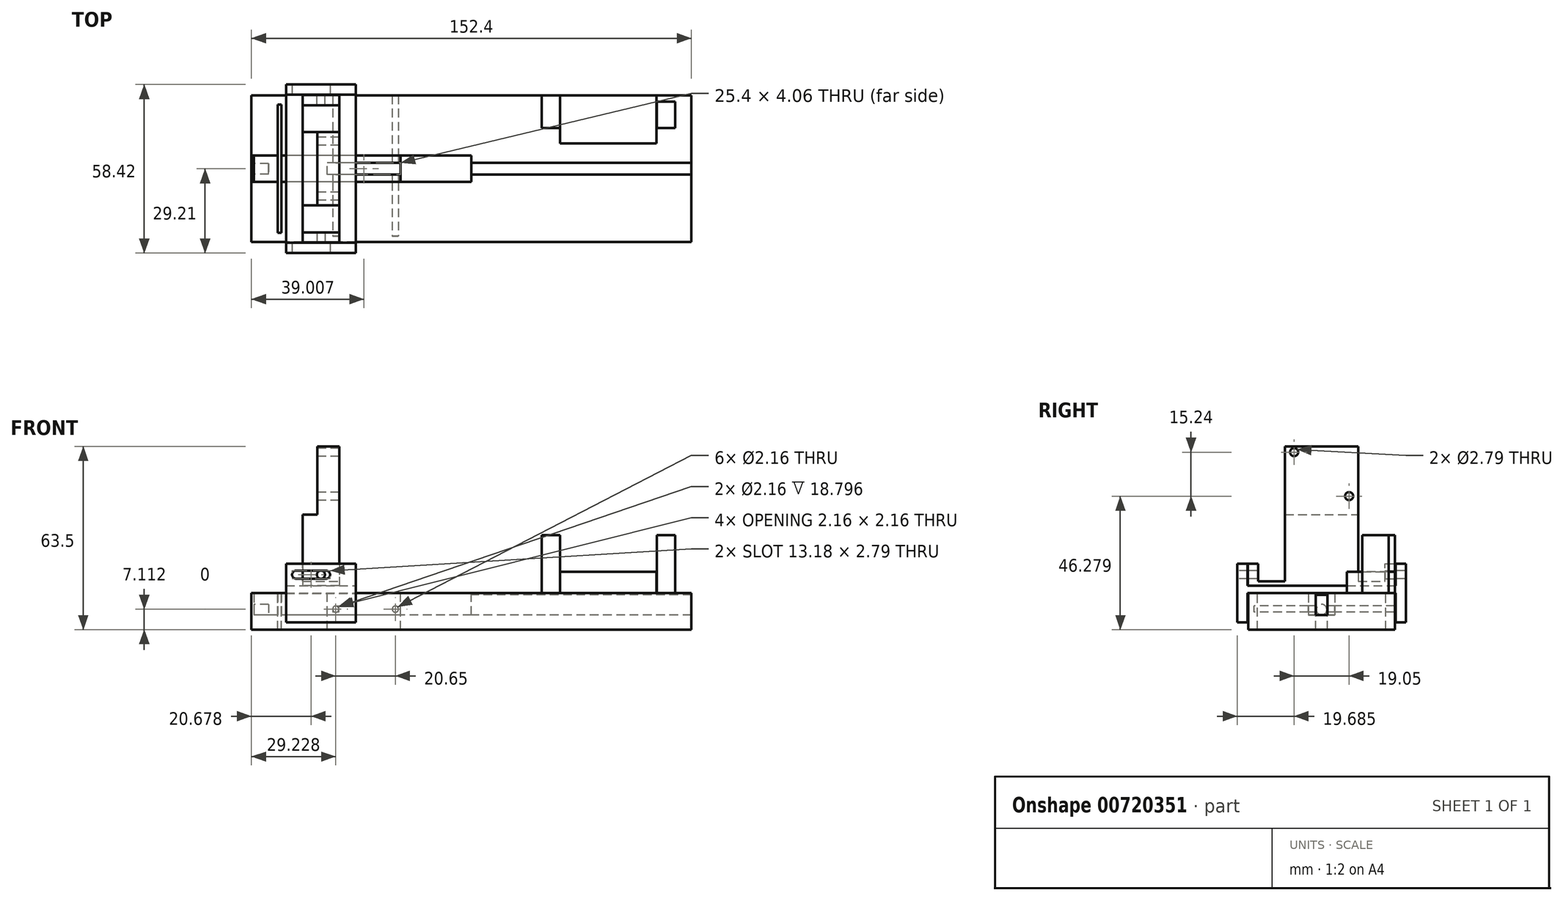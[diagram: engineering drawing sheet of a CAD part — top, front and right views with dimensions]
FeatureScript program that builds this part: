
annotation { "Feature Type Name" : "Feature", "Feature Type Description" : "" }
export const myFeature = defineFeature(function(context is Context, id is Id, definition is map)
    precondition{}
    {
        {
            var Q0;
            Q0=qCreatedBy(makeId("Top.planeOp"),FACE);
            var sketch = newSketch(context, id + "F0", { "sketchPlane" : qUnion([Q0])});
            skLineSegment(sketch, "E0.bottom", {"start": v(76.2, -25.4) * mm, "end": v(-76.2, -25.4) * mm});
            skLineSegment(sketch, "E0.top", {"start": v(76.2, 25.4) * mm, "end": v(-76.2, 25.4) * mm});
            skLineSegment(sketch, "E0.left", {"start": v(76.2, -25.4) * mm, "end": v(76.2, 25.4) * mm});
            skLineSegment(sketch, "E0.right", {"start": v(-76.2, -25.4) * mm, "end": v(-76.2, 25.4) * mm});
            skPoint(sketch, "E0.middle", {"position": v(0, 0) * mm});
            skSolve(sketch);
        }
        {
            var Q0;
            Q0 = qSketchRegion(id + "F0", true);
            extrude(context, id + "F1", {"entities" : qUnion([Q0]), "depth" : 12.7 * mm, "offsetDistance" : 25.4 * mm});
        }
        {
            var Q0;
            Q0=makeQuery(id+"F1.opExtrude","CAP_FACE",FACE,{"disambiguationData":[OSD([sQuery(id+"F0.wireOp",EDGE,"E0.bottom"),sQuery(id+"F0.wireOp",EDGE,"E0.top"),sQuery(id+"F0.wireOp",EDGE,"E0.left"),sQuery(id+"F0.wireOp",EDGE,"E0.right")])],"isStart":false});
            var sketch = newSketch(context, id + "F2", { "sketchPlane" : qUnion([Q0])});
            skLineSegment(sketch, "E1.bottom", {"start": v(-76.2, -2.03) * mm, "end": v(76.2, -2.03) * mm});
            skLineSegment(sketch, "E1.top", {"start": v(-76.2, 2.03) * mm, "end": v(76.2, 2.03) * mm});
            skLineSegment(sketch, "E1.left", {"start": v(-76.2, -2.03) * mm, "end": v(-76.2, 2.03) * mm});
            skLineSegment(sketch, "E1.right", {"start": v(76.2, -2.03) * mm, "end": v(76.2, 2.03) * mm});
            skPoint(sketch, "E1.middle", {"position": v(0, 0) * mm});
            skSolve(sketch);
        }
        {
            var Q0;
            Q0 = qSketchRegion(id + "F2", true);
            extrude(context, id + "F3", {"entities" : qUnion([Q0]), "operationType" : NewBodyOperationType.REMOVE, "oppositeDirection" : true, "depth" : 7.62 * mm, "offsetDistance" : 25.4 * mm});
        }
        {
            var Q0;
            Q0=makeQuery(id+"F3.boolean.opBoolean","COPY",FACE,{"derivedFrom":makeQuery(id+"F3.opExtrude","CAP_FACE",FACE,{"disambiguationData":[OSD([sQuery(id+"F2.wireOp",EDGE,"E1.bottom"),sQuery(id+"F2.wireOp",EDGE,"E1.top"),sQuery(id+"F2.wireOp",EDGE,"E1.left"),sQuery(id+"F2.wireOp",EDGE,"E1.right")])],"isStart":false})});
            var sketch = newSketch(context, id + "F4", { "sketchPlane" : qUnion([Q0])});
            skPoint(sketch, "E2.middle", {"position": v(0, 0) * mm});
            skLineSegment(sketch, "E3.bottom", {"start": v(76.2, -2.02) * mm, "end": v(-49.28, -2.02) * mm});
            skLineSegment(sketch, "E3.top", {"start": v(76.2, 2.02) * mm, "end": v(-49.28, 2.02) * mm});
            skLineSegment(sketch, "E3.left", {"start": v(76.2, -2.02) * mm, "end": v(76.2, 2.02) * mm});
            skLineSegment(sketch, "E3.right", {"start": v(-49.28, -2.02) * mm, "end": v(-49.28, 2.02) * mm});
            skPoint(sketch, "E3.middle", {"position": v(13.46, 0) * mm});
            skSolve(sketch);
        }
        {
            var Q0;
            Q0 = qSketchRegion(id + "F4", true);
            extrude(context, id + "F5", {"entities" : qUnion([Q0]), "depth" : 7.04 * mm, "offsetDistance" : 25.4 * mm});
        }
        {
            var Q0;
            {var subQ0=sQuery(id+"F0.wireOp",EDGE,"E0.top");var subQ1=sQuery(id+"F0.wireOp",EDGE,"E0.left");var subQ2=sQuery(id+"F0.wireOp",EDGE,"E0.right");Q0=makeQuery(id+"F3.boolean.opBoolean","SPLIT",FACE,{"disambiguationData":[TD([makeQuery(id+"F1.opExtrude","SWEPT_FACE",FACE,{"disambiguationData":[OSD([subQ0])]})])],"derivedFrom":makeQuery(id+"F1.opExtrude","CAP_FACE",FACE,{"disambiguationData":[OSD([sQuery(id+"F0.wireOp",EDGE,"E0.bottom"),subQ0,subQ1,subQ2])],"isStart":false})});}
            var sketch = newSketch(context, id + "F6", { "sketchPlane" : qUnion([Q0])});
            skLineSegment(sketch, "E4.bottom", {"start": v(0, -4.57) * mm, "end": v(-76.2, -4.57) * mm});
            skLineSegment(sketch, "E4.top", {"start": v(0, 4.57) * mm, "end": v(-76.2, 4.57) * mm});
            skLineSegment(sketch, "E4.left", {"start": v(0, -4.57) * mm, "end": v(0, 4.57) * mm});
            skLineSegment(sketch, "E4.right", {"start": v(-76.2, -4.57) * mm, "end": v(-76.2, 4.57) * mm});
            skPoint(sketch, "E4.middle", {"position": v(-38.1, 0) * mm});
            skSolve(sketch);
        }
        {
            var Q0;
            Q0 = qSketchRegion(id + "F6", true);
            extrude(context, id + "F7", {"entities" : qUnion([Q0]), "operationType" : NewBodyOperationType.REMOVE, "oppositeDirection" : true, "depth" : 7.62 * mm, "offsetDistance" : 25.4 * mm});
        }
        {
            var Q0;
            Q0=makeQuery(id+"F7.boolean.opBoolean","MERGE",FACE,{"derivedFrom":[makeQuery(id+"F3.boolean.opBoolean","COPY",FACE,{"derivedFrom":makeQuery(id+"F3.opExtrude","CAP_FACE",FACE,{"disambiguationData":[OSD([sQuery(id+"F2.wireOp",EDGE,"E1.bottom"),sQuery(id+"F2.wireOp",EDGE,"E1.top"),sQuery(id+"F2.wireOp",EDGE,"E1.left"),sQuery(id+"F2.wireOp",EDGE,"E1.right")])],"isStart":false})}),makeQuery(id+"F7.opExtrude","CAP_FACE",FACE,{"disambiguationData":[OSD([sQuery(id+"F6.wireOp",EDGE,"E4.bottom"),sQuery(id+"F6.wireOp",EDGE,"E4.top"),sQuery(id+"F6.wireOp",EDGE,"E4.left"),sQuery(id+"F6.wireOp",EDGE,"E4.right")])],"isStart":false})]});
            var sketch = newSketch(context, id + "F8", { "sketchPlane" : qUnion([Q0])});
            skLineSegment(sketch, "E5.bottom", {"start": v(-24.5, 4.56) * mm, "end": v(-75.3, 4.56) * mm});
            skLineSegment(sketch, "E5.top", {"start": v(-24.5, -4.55) * mm, "end": v(-75.3, -4.55) * mm});
            skLineSegment(sketch, "E5.left", {"start": v(-24.5, 4.56) * mm, "end": v(-24.5, -4.55) * mm});
            skLineSegment(sketch, "E5.right", {"start": v(-75.3, 4.56) * mm, "end": v(-75.3, -4.55) * mm});
            skSolve(sketch);
        }
        {
            var Q0;
            Q0 = qSketchRegion(id + "F8", true);
            extrude(context, id + "F9", {"entities" : qUnion([Q0]), "depth" : 7.37 * mm, "offsetDistance" : 25.4 * mm});
        }
        {
            var Q0;
            {var subQ0=sQuery(id+"F0.wireOp",EDGE,"E0.top");var subQ1=sQuery(id+"F0.wireOp",EDGE,"E0.left");var subQ2=sQuery(id+"F0.wireOp",EDGE,"E0.right");Q0=makeQuery(id+"F3.boolean.opBoolean","SPLIT",FACE,{"disambiguationData":[TD([makeQuery(id+"F1.opExtrude","SWEPT_FACE",FACE,{"disambiguationData":[OSD([subQ0])]})])],"derivedFrom":makeQuery(id+"F1.opExtrude","CAP_FACE",FACE,{"disambiguationData":[OSD([sQuery(id+"F0.wireOp",EDGE,"E0.bottom"),subQ0,subQ1,subQ2])],"isStart":false})});}
            var sketch = newSketch(context, id + "F10", { "sketchPlane" : qUnion([Q0])});
            skLineSegment(sketch, "E6.bottom", {"start": v(-65.81, -22.23) * mm, "end": v(-67.08, -22.23) * mm});
            skLineSegment(sketch, "E6.top", {"start": v(-65.81, 22.23) * mm, "end": v(-67.08, 22.23) * mm});
            skLineSegment(sketch, "E6.left", {"start": v(-65.81, -22.23) * mm, "end": v(-65.81, 22.23) * mm});
            skLineSegment(sketch, "E6.right", {"start": v(-67.08, -22.23) * mm, "end": v(-67.08, 22.23) * mm});
            skPoint(sketch, "E6.middle", {"position": v(-66.45, 0) * mm});
            skSolve(sketch);
        }
        {
            var Q0;
            Q0 = qSketchRegion(id + "F10", true);
            extrude(context, id + "F11", {"entities" : qUnion([Q0]), "operationType" : NewBodyOperationType.REMOVE, "oppositeDirection" : true, "depth" : 25.4 * mm, "offsetDistance" : 25.4 * mm});
        }
        {
            var Q0;
            {var subQ0=sQuery(id+"F0.wireOp",EDGE,"E0.top");var subQ1=sQuery(id+"F0.wireOp",EDGE,"E0.left");var subQ2=sQuery(id+"F0.wireOp",EDGE,"E0.right");Q0=makeQuery(id+"F3.boolean.opBoolean","SPLIT",FACE,{"disambiguationData":[TD([makeQuery(id+"F1.opExtrude","SWEPT_FACE",FACE,{"disambiguationData":[OSD([subQ0])]})])],"derivedFrom":makeQuery(id+"F1.opExtrude","CAP_FACE",FACE,{"disambiguationData":[OSD([sQuery(id+"F0.wireOp",EDGE,"E0.bottom"),subQ0,subQ1,subQ2])],"isStart":false})});}
            var sketch = newSketch(context, id + "F12", { "sketchPlane" : qUnion([Q0])});
            skLineSegment(sketch, "E7.bottom", {"start": v(30.66, 14.12) * mm, "end": v(24.3, 14.12) * mm});
            skLineSegment(sketch, "E7.top", {"start": v(30.66, 25.4) * mm, "end": v(24.3, 25.4) * mm});
            skLineSegment(sketch, "E7.left", {"start": v(30.66, 14.12) * mm, "end": v(30.66, 25.4) * mm});
            skLineSegment(sketch, "E7.right", {"start": v(24.3, 14.12) * mm, "end": v(24.3, 25.4) * mm});
            skLineSegment(sketch, "E8.bottom", {"start": v(64.2, 14.12) * mm, "end": v(70.6, 14.12) * mm});
            skLineSegment(sketch, "E8.top", {"start": v(64.2, 23.2) * mm, "end": v(70.6, 23.2) * mm});
            skLineSegment(sketch, "E8.left", {"start": v(64.2, 14.12) * mm, "end": v(64.2, 23.2) * mm});
            skLineSegment(sketch, "E8.right", {"start": v(70.6, 14.12) * mm, "end": v(70.6, 23.2) * mm});
            skSolve(sketch);
        }
        {
            var Q0;
            Q0 = qSketchRegion(id + "F12", true);
            extrude(context, id + "F13", {"entities" : qUnion([Q0]), "operationType" : NewBodyOperationType.ADD, "depth" : 20.02 * mm, "offsetDistance" : 25.4 * mm});
        }
        {
            var Q0;
            {var subQ0=sQuery(id+"F0.wireOp",EDGE,"E0.top");var subQ1=sQuery(id+"F0.wireOp",EDGE,"E0.left");var subQ2=sQuery(id+"F0.wireOp",EDGE,"E0.right");Q0=makeQuery(id+"F3.boolean.opBoolean","SPLIT",FACE,{"disambiguationData":[TD([makeQuery(id+"F1.opExtrude","SWEPT_FACE",FACE,{"disambiguationData":[OSD([subQ0])]})])],"derivedFrom":makeQuery(id+"F1.opExtrude","CAP_FACE",FACE,{"disambiguationData":[OSD([sQuery(id+"F0.wireOp",EDGE,"E0.bottom"),subQ0,subQ1,subQ2])],"isStart":false})});}
            var sketch = newSketch(context, id + "F14", { "sketchPlane" : qUnion([Q0])});
            skLineSegment(sketch, "E9.bottom", {"start": v(30.66, 25.4) * mm, "end": v(64.13, 25.4) * mm});
            skLineSegment(sketch, "E9.top", {"start": v(30.66, 8.77) * mm, "end": v(64.13, 8.77) * mm});
            skLineSegment(sketch, "E9.left", {"start": v(30.66, 25.4) * mm, "end": v(30.66, 8.77) * mm});
            skLineSegment(sketch, "E9.right", {"start": v(64.13, 25.4) * mm, "end": v(64.13, 8.77) * mm});
            skSolve(sketch);
        }
        {
            var Q0;
            Q0 = qSketchRegion(id + "F14", true);
            extrude(context, id + "F15", {"entities" : qUnion([Q0]), "operationType" : NewBodyOperationType.ADD, "depth" : 7.32 * mm, "offsetDistance" : 25.4 * mm});
        }
        {
            var Q0;
            Q0=makeQuery(id+"F9.opExtrude","CAP_FACE",FACE,{"disambiguationData":[OSD([sQuery(id+"F8.wireOp",EDGE,"E5.bottom"),sQuery(id+"F8.wireOp",EDGE,"E5.top"),sQuery(id+"F8.wireOp",EDGE,"E5.left"),sQuery(id+"F8.wireOp",EDGE,"E5.right")])],"isStart":false});
            var sketch = newSketch(context, id + "F16", { "sketchPlane" : qUnion([Q0])});
            skPoint(sketch, "E10.startSnap0", {"position": v(-24.5, 0) * mm});
            skLineSegment(sketch, "E11.bottom", {"start": v(-24.5, -2.03) * mm, "end": v(-49.9, -2.03) * mm});
            skLineSegment(sketch, "E11.top", {"start": v(-24.5, 2.03) * mm, "end": v(-49.9, 2.03) * mm});
            skLineSegment(sketch, "E11.left", {"start": v(-24.5, -2.03) * mm, "end": v(-24.5, 2.03) * mm});
            skLineSegment(sketch, "E11.right", {"start": v(-49.9, -2.03) * mm, "end": v(-49.9, 2.03) * mm});
            skPoint(sketch, "E11.middle", {"position": v(-37.2, 0) * mm});
            skSolve(sketch);
        }
        {
            var Q0;
            Q0 = qSketchRegion(id + "F16", true);
            extrude(context, id + "F17", {"entities" : qUnion([Q0]), "operationType" : NewBodyOperationType.REMOVE, "oppositeDirection" : true, "depth" : 25.4 * mm, "offsetDistance" : 25.4 * mm});
        }
        {
            var Q0;
            Q0=makeQuery(id+"F9.opExtrude","SWEPT_FACE",FACE,{"disambiguationData":[OSD([sQuery(id+"F8.wireOp",EDGE,"E5.right")])]});
            var sketch = newSketch(context, id + "F18", { "sketchPlane" : qUnion([Q0])});
            skCircle(sketch, "E12", {"center": v(0, 6.93) * mm, "radius": 1.84 * mm});
            skSolve(sketch);
        }
        {
            var Q0;
            Q0 = qSketchRegion(id + "F18", true);
            extrude(context, id + "F19", {"entities" : qUnion([Q0]), "operationType" : NewBodyOperationType.REMOVE, "oppositeDirection" : true, "depth" : 5.08 * mm, "offsetDistance" : 25.4 * mm});
        }
        {
            var Q0;
            Q0=makeQuery(id+"F17.boolean.opBoolean","COPY",FACE,{"derivedFrom":makeQuery(id+"F17.opExtrude","SWEPT_FACE",FACE,{"disambiguationData":[OSD([sQuery(id+"F16.wireOp",EDGE,"E11.top")])]})});
            var sketch = newSketch(context, id + "F20", { "sketchPlane" : qUnion([Q0])});
            skCircle(sketch, "E13", {"center": v(-46.97, 7.11) * mm, "radius": 1.08 * mm});
            skCircle(sketch, "E14", {"center": v(-26.32, 7.11) * mm, "radius": 1.08 * mm});
            skSolve(sketch);
        }
        {
            var Q0;
            Q0 = qSketchRegion(id + "F20", true);
            extrude(context, id + "F21", {"entities" : qUnion([Q0]), "operationType" : NewBodyOperationType.REMOVE, "endBound" : BoundingType.SYMMETRIC, "oppositeDirection" : true, "depth" : 50.8 * mm, "offsetDistance" : 25.4 * mm});
        }
        {
            var Q0;
            {var subQ0=sQuery(id+"F0.wireOp",EDGE,"E0.top");var subQ1=sQuery(id+"F0.wireOp",EDGE,"E0.left");var subQ2=sQuery(id+"F0.wireOp",EDGE,"E0.right");Q0=makeQuery(id+"F3.boolean.opBoolean","SPLIT",FACE,{"disambiguationData":[TD([makeQuery(id+"F1.opExtrude","SWEPT_FACE",FACE,{"disambiguationData":[OSD([subQ0])]})])],"derivedFrom":makeQuery(id+"F1.opExtrude","CAP_FACE",FACE,{"disambiguationData":[OSD([sQuery(id+"F0.wireOp",EDGE,"E0.bottom"),subQ0,subQ1,subQ2])],"isStart":false})});}
            var sketch = newSketch(context, id + "F22", { "sketchPlane" : qUnion([Q0])});
            skLineSegment(sketch, "E15.bottom", {"start": v(-40.05, -29.21) * mm, "end": v(-64.18, -29.21) * mm});
            skLineSegment(sketch, "E15.top", {"start": v(-40.05, 29.2) * mm, "end": v(-64.18, 29.2) * mm});
            skLineSegment(sketch, "E15.left", {"start": v(-40.05, -29.21) * mm, "end": v(-40.05, 29.2) * mm});
            skLineSegment(sketch, "E15.right", {"start": v(-64.18, -29.21) * mm, "end": v(-64.18, 29.2) * mm});
            skPoint(sketch, "E15.middle", {"position": v(-52.12, 0) * mm});
            skSolve(sketch);
        }
        {
            var Q0;
            Q0 = qSketchRegion(id + "F22", true);
            extrude(context, id + "F23", {"entities" : qUnion([Q0]), "depth" : 2.54 * mm, "offsetDistance" : 25.4 * mm});
        }
        {
            var Q0;
            Q0=makeQuery(id+"F23.opExtrude","CAP_FACE",FACE,{"disambiguationData":[OSD([sQuery(id+"F22.wireOp",EDGE,"E15.bottom"),sQuery(id+"F22.wireOp",EDGE,"E15.top"),sQuery(id+"F22.wireOp",EDGE,"E15.left"),sQuery(id+"F22.wireOp",EDGE,"E15.right")])],"isStart":true});
            var sketch = newSketch(context, id + "F24", { "sketchPlane" : qUnion([Q0])});
            skLineSegment(sketch, "E16.bottom", {"start": v(-64.18, 29.21) * mm, "end": v(-40.05, 29.21) * mm});
            skLineSegment(sketch, "E16.top", {"start": v(-64.18, 25.64) * mm, "end": v(-40.05, 25.64) * mm});
            skLineSegment(sketch, "E16.left", {"start": v(-64.18, 29.21) * mm, "end": v(-64.18, 25.64) * mm});
            skLineSegment(sketch, "E16.right", {"start": v(-40.05, 29.21) * mm, "end": v(-40.05, 25.64) * mm});
            skLineSegment(sketch, "E17.bottom", {"start": v(-64.18, -29.2) * mm, "end": v(-40.05, -29.2) * mm});
            skLineSegment(sketch, "E17.top", {"start": v(-64.18, -25.65) * mm, "end": v(-40.05, -25.65) * mm});
            skLineSegment(sketch, "E17.left", {"start": v(-64.18, -29.2) * mm, "end": v(-64.18, -25.65) * mm});
            skLineSegment(sketch, "E17.right", {"start": v(-40.05, -29.2) * mm, "end": v(-40.05, -25.65) * mm});
            skSolve(sketch);
        }
        {
            var Q0;
            Q0 = qSketchRegion(id + "F24", true);
            extrude(context, id + "F25", {"entities" : qUnion([Q0]), "operationType" : NewBodyOperationType.ADD, "endBound" : BoundingType.SYMMETRIC, "depth" : 20.32 * mm, "offsetDistance" : 25.4 * mm});
        }
        {
            var Q0;
            {var subQ0=sQuery(id+"F22.wireOp",EDGE,"E15.right");var subQ1=sQuery(id+"F22.wireOp",EDGE,"E15.left");var subQ4=sQuery(id+"F24.wireOp",EDGE,"E17.top");Q0=makeQuery(id+"F25.boolean.opBoolean","SPLIT",FACE,{"disambiguationData":[TD([makeQuery(id+"F23.opExtrude","CAP_FACE",FACE,{"disambiguationData":[OSD([sQuery(id+"F22.wireOp",EDGE,"E15.bottom"),sQuery(id+"F22.wireOp",EDGE,"E15.top"),subQ1,subQ0])],"isStart":false})])],"derivedFrom":makeQuery(id+"F25.opExtrude","SWEPT_FACE",FACE,{"disambiguationData":[OSD([subQ4])]})});}
            var sketch = newSketch(context, id + "F26", { "sketchPlane" : qUnion([Q0])});
            skCircle(sketch, "E18", {"center": v(-60.72, 19.05) * mm, "radius": 1.4 * mm});
            skPoint(sketch, "E18.centerSnap0", {"position": v(-64.18, 19.05) * mm});
            skCircle(sketch, "E19", {"center": v(-50.33, 19.05) * mm, "radius": 1.4 * mm});
            skLineSegment(sketch, "E20.bottom", {"start": v(-60.72, 20.45) * mm, "end": v(-50.33, 20.45) * mm});
            skLineSegment(sketch, "E20.top", {"start": v(-60.72, 17.65) * mm, "end": v(-50.33, 17.65) * mm});
            skLineSegment(sketch, "E20.left", {"start": v(-60.72, 20.45) * mm, "end": v(-60.72, 17.65) * mm});
            skLineSegment(sketch, "E20.right", {"start": v(-50.33, 20.45) * mm, "end": v(-50.33, 17.65) * mm});
            skSolve(sketch);
        }
        {
            var Q0;
            Q0 = qSketchRegion(id + "F26", true);
            extrude(context, id + "F27", {"entities" : qUnion([Q0]), "operationType" : NewBodyOperationType.REMOVE, "endBound" : BoundingType.SYMMETRIC, "oppositeDirection" : true, "depth" : 280.42 * mm, "offsetDistance" : 25.4 * mm});
        }
        {
            var Q0;
            Q0=makeQuery(id+"F23.opExtrude","CAP_FACE",FACE,{"disambiguationData":[OSD([sQuery(id+"F22.wireOp",EDGE,"E15.bottom"),sQuery(id+"F22.wireOp",EDGE,"E15.top"),sQuery(id+"F22.wireOp",EDGE,"E15.left"),sQuery(id+"F22.wireOp",EDGE,"E15.right")])],"isStart":false});
            var sketch = newSketch(context, id + "F28", { "sketchPlane" : qUnion([Q0])});
            skLineSegment(sketch, "E21.bottom", {"start": v(-45.77, -25.52) * mm, "end": v(-58.47, -25.52) * mm});
            skLineSegment(sketch, "E21.top", {"start": v(-45.77, 25.52) * mm, "end": v(-58.47, 25.52) * mm});
            skLineSegment(sketch, "E21.left", {"start": v(-45.77, -25.52) * mm, "end": v(-45.77, 25.52) * mm});
            skLineSegment(sketch, "E21.right", {"start": v(-58.47, -25.52) * mm, "end": v(-58.47, 25.52) * mm});
            skPoint(sketch, "E21.middle", {"position": v(-52.12, 0) * mm});
            skPoint(sketch, "E21.middle.positionSnap0", {"position": v(-52.12, 25.65) * mm});
            skPoint(sketch, "E21.centerSnap0", {"position": v(-52.12, 25.65) * mm});
            skSolve(sketch);
        }
        {
            var Q0;
            Q0 = qSketchRegion(id + "F28", true);
            extrude(context, id + "F29", {"entities" : qUnion([Q0]), "depth" : 7.62 * mm, "offsetDistance" : 25.4 * mm});
        }
        {
            var Q0;
            Q0=makeQuery(id+"F29.opExtrude","CAP_FACE",FACE,{"disambiguationData":[OSD([sQuery(id+"F28.wireOp",EDGE,"E21.bottom"),sQuery(id+"F28.wireOp",EDGE,"E21.top"),sQuery(id+"F28.wireOp",EDGE,"E21.left"),sQuery(id+"F28.wireOp",EDGE,"E21.right")])],"isStart":false});
            var sketch = newSketch(context, id + "F30", { "sketchPlane" : qUnion([Q0])});
            skLineSegment(sketch, "E22.bottom", {"start": v(-45.77, -22.01) * mm, "end": v(-58.47, -22.01) * mm});
            skLineSegment(sketch, "E22.top", {"start": v(-45.77, 22.01) * mm, "end": v(-58.47, 22.01) * mm});
            skLineSegment(sketch, "E22.left", {"start": v(-45.77, -22.01) * mm, "end": v(-45.77, 22.01) * mm});
            skLineSegment(sketch, "E22.right", {"start": v(-58.47, -22.01) * mm, "end": v(-58.47, 22.01) * mm});
            skPoint(sketch, "E22.middle", {"position": v(-52.12, 0) * mm});
            skPoint(sketch, "E22.middle.positionSnap0", {"position": v(-52.12, 25.52) * mm});
            skPoint(sketch, "E22.middle.positionSnap1", {"position": v(-45.77, 0) * mm});
            skPoint(sketch, "E22.centerSnap0", {"position": v(-52.12, 25.52) * mm});
            skPoint(sketch, "E22.centerSnap1", {"position": v(-45.77, 0) * mm});
            skSolve(sketch);
        }
        {
            var Q0;
            Q0 = qSketchRegion(id + "F30", true);
            extrude(context, id + "F31", {"entities" : qUnion([Q0]), "operationType" : NewBodyOperationType.REMOVE, "oppositeDirection" : true, "depth" : 5.08 * mm, "offsetDistance" : 25.4 * mm});
        }
        {
            var Q0;
            Q0=makeQuery(id+"F31.boolean.opBoolean","COPY",FACE,{"derivedFrom":makeQuery(id+"F31.opExtrude","CAP_FACE",FACE,{"disambiguationData":[OSD([sQuery(id+"F30.wireOp",EDGE,"E22.bottom"),sQuery(id+"F30.wireOp",EDGE,"E22.top"),sQuery(id+"F30.wireOp",EDGE,"E22.left"),sQuery(id+"F30.wireOp",EDGE,"E22.right")])],"isStart":false})});
            var sketch = newSketch(context, id + "F32", { "sketchPlane" : qUnion([Q0])});
            skLineSegment(sketch, "E23.bottom", {"start": v(-58.47, -12.7) * mm, "end": v(-45.77, -12.7) * mm});
            skLineSegment(sketch, "E23.top", {"start": v(-58.47, 12.7) * mm, "end": v(-45.77, 12.7) * mm});
            skLineSegment(sketch, "E23.left", {"start": v(-58.47, -12.7) * mm, "end": v(-58.47, 12.7) * mm});
            skLineSegment(sketch, "E23.right", {"start": v(-45.77, -12.7) * mm, "end": v(-45.77, 12.7) * mm});
            skPoint(sketch, "E23.middle", {"position": v(-52.12, 0) * mm});
            skPoint(sketch, "E23.middle.positionSnap0", {"position": v(-45.77, 0) * mm});
            skPoint(sketch, "E23.middle.positionSnap1", {"position": v(-52.12, 22.01) * mm});
            skPoint(sketch, "E23.centerSnap0", {"position": v(-45.77, 0) * mm});
            skPoint(sketch, "E23.centerSnap1", {"position": v(-52.12, 22.01) * mm});
            skSolve(sketch);
        }
        {
            var Q0;
            Q0 = qSketchRegion(id + "F32", true);
            extrude(context, id + "F33", {"entities" : qUnion([Q0]), "operationType" : NewBodyOperationType.ADD, "depth" : 45.72 * mm, "offsetDistance" : 25.4 * mm});
        }
        {
            var Q0;
            Q0=makeQuery(id+"F33.boolean.opBoolean","MERGE",FACE,{"derivedFrom":[makeQuery(id+"F29.opExtrude","SWEPT_FACE",FACE,{"disambiguationData":[OSD([sQuery(id+"F28.wireOp",EDGE,"E21.right")])]}),makeQuery(id+"F33.opExtrude","SWEPT_FACE",FACE,{"disambiguationData":[OSD([sQuery(id+"F32.wireOp",EDGE,"E23.left")])]})]});
            var sketch = newSketch(context, id + "F34", { "sketchPlane" : qUnion([Q0])});
            skCircle(sketch, "E24", {"center": v(9.52, 61.52) * mm, "radius": 1.4 * mm});
            skCircle(sketch, "E25", {"center": v(-9.52, 46.28) * mm, "radius": 1.4 * mm});
            skSolve(sketch);
        }
        {
            var Q0;
            Q0 = qSketchRegion(id + "F34", true);
            extrude(context, id + "F35", {"entities" : qUnion([Q0]), "operationType" : NewBodyOperationType.REMOVE, "oppositeDirection" : true, "depth" : 25.4 * mm, "offsetDistance" : 25.4 * mm});
        }
        {
            var Q0;
            Q0=makeQuery(id+"F33.opExtrude","CAP_FACE",FACE,{"disambiguationData":[OSD([sQuery(id+"F32.wireOp",EDGE,"E23.bottom"),sQuery(id+"F32.wireOp",EDGE,"E23.top"),sQuery(id+"F32.wireOp",EDGE,"E23.left"),sQuery(id+"F32.wireOp",EDGE,"E23.right")])],"isStart":false});
            var sketch = newSketch(context, id + "F36", { "sketchPlane" : qUnion([Q0])});
            skLineSegment(sketch, "E26.bottom", {"start": v(-58.47, 12.7) * mm, "end": v(-53.4, 12.7) * mm});
            skLineSegment(sketch, "E26.top", {"start": v(-58.47, -12.7) * mm, "end": v(-53.4, -12.7) * mm});
            skLineSegment(sketch, "E26.left", {"start": v(-58.47, 12.7) * mm, "end": v(-58.47, -12.7) * mm});
            skLineSegment(sketch, "E26.right", {"start": v(-53.4, 12.7) * mm, "end": v(-53.4, -12.7) * mm});
            skSolve(sketch);
        }
        {
            var Q0;
            Q0 = qSketchRegion(id + "F36", true);
            extrude(context, id + "F37", {"entities" : qUnion([Q0]), "operationType" : NewBodyOperationType.REMOVE, "oppositeDirection" : true, "depth" : 23.62 * mm, "offsetDistance" : 25.4 * mm});
        }
        {
            var Q0;
            Q0=makeQuery(id+"F29.opExtrude","SWEPT_FACE",FACE,{"disambiguationData":[OSD([sQuery(id+"F28.wireOp",EDGE,"E21.bottom")])]});
            var sketch = newSketch(context, id + "F38", { "sketchPlane" : qUnion([Q0])});
            skPoint(sketch, "E27.centerSnap0", {"position": v(-45.77, 19.05) * mm});
            skCircle(sketch, "E28", {"center": v(-52.12, 19.05) * mm, "radius": 1.4 * mm});
            skPoint(sketch, "E28.centerSnap0", {"position": v(-52.12, 22.86) * mm});
            skSolve(sketch);
        }
        {
            var Q0;
            Q0=makeQuery(id+"F29.opExtrude","SWEPT_FACE",FACE,{"disambiguationData":[OSD([sQuery(id+"F28.wireOp",EDGE,"E21.top")])]});
            var sketch = newSketch(context, id + "F39", { "sketchPlane" : qUnion([Q0])});
            skCircle(sketch, "E29", {"center": v(52.12, 19.05) * mm, "radius": 1.4 * mm});
            skPoint(sketch, "E29.centerSnap0", {"position": v(52.12, 22.86) * mm});
            skPoint(sketch, "E29.centerSnap1", {"position": v(58.47, 19.05) * mm});
            skSolve(sketch);
        }
        {
            var Q0;
            {var subQ0=sQuery(id+"F30.wireOp",EDGE,"E22.top");Q0=makeQuery(id+"F33.boolean.opBoolean","SPLIT",FACE,{"disambiguationData":[TD([makeQuery(id+"F31.boolean.opBoolean","COPY",FACE,{"derivedFrom":makeQuery(id+"F31.opExtrude","SWEPT_FACE",FACE,{"disambiguationData":[OSD([subQ0])]})})])],"derivedFrom":makeQuery(id+"F31.boolean.opBoolean","COPY",FACE,{"derivedFrom":makeQuery(id+"F31.opExtrude","CAP_FACE",FACE,{"disambiguationData":[OSD([sQuery(id+"F30.wireOp",EDGE,"E22.bottom"),subQ0,sQuery(id+"F30.wireOp",EDGE,"E22.left"),sQuery(id+"F30.wireOp",EDGE,"E22.right")])],"isStart":false})})});}
            var Q1;
            {var subQ0=sQuery(id+"F30.wireOp",EDGE,"E22.bottom");Q1=makeQuery(id+"F33.boolean.opBoolean","SPLIT",FACE,{"disambiguationData":[TD([makeQuery(id+"F31.boolean.opBoolean","COPY",FACE,{"derivedFrom":makeQuery(id+"F31.opExtrude","SWEPT_FACE",FACE,{"disambiguationData":[OSD([subQ0])]})})])],"derivedFrom":makeQuery(id+"F31.boolean.opBoolean","COPY",FACE,{"derivedFrom":makeQuery(id+"F31.opExtrude","CAP_FACE",FACE,{"disambiguationData":[OSD([subQ0,sQuery(id+"F30.wireOp",EDGE,"E22.top"),sQuery(id+"F30.wireOp",EDGE,"E22.left"),sQuery(id+"F30.wireOp",EDGE,"E22.right")])],"isStart":false})})});}
            extrude(context, id + "F40", {"entities" : qUnion([Q0, Q1]), "operationType" : NewBodyOperationType.REMOVE, "oppositeDirection" : true, "depth" : 1.02 * mm, "offsetDistance" : 25.4 * mm});
        }
        {
            var Q0;
            Q0 = qSketchRegion(id + "F38", true);
            extrude(context, id + "F41", {"entities" : qUnion([Q0]), "operationType" : NewBodyOperationType.REMOVE, "oppositeDirection" : true, "depth" : 8.56 * mm, "offsetDistance" : 25.4 * mm});
        }
        {
            var Q0;
            Q0 = qSketchRegion(id + "F39", true);
            extrude(context, id + "F42", {"entities" : qUnion([Q0]), "operationType" : NewBodyOperationType.REMOVE, "oppositeDirection" : true, "depth" : 7.54 * mm, "offsetDistance" : 25.4 * mm});
        }
    });
